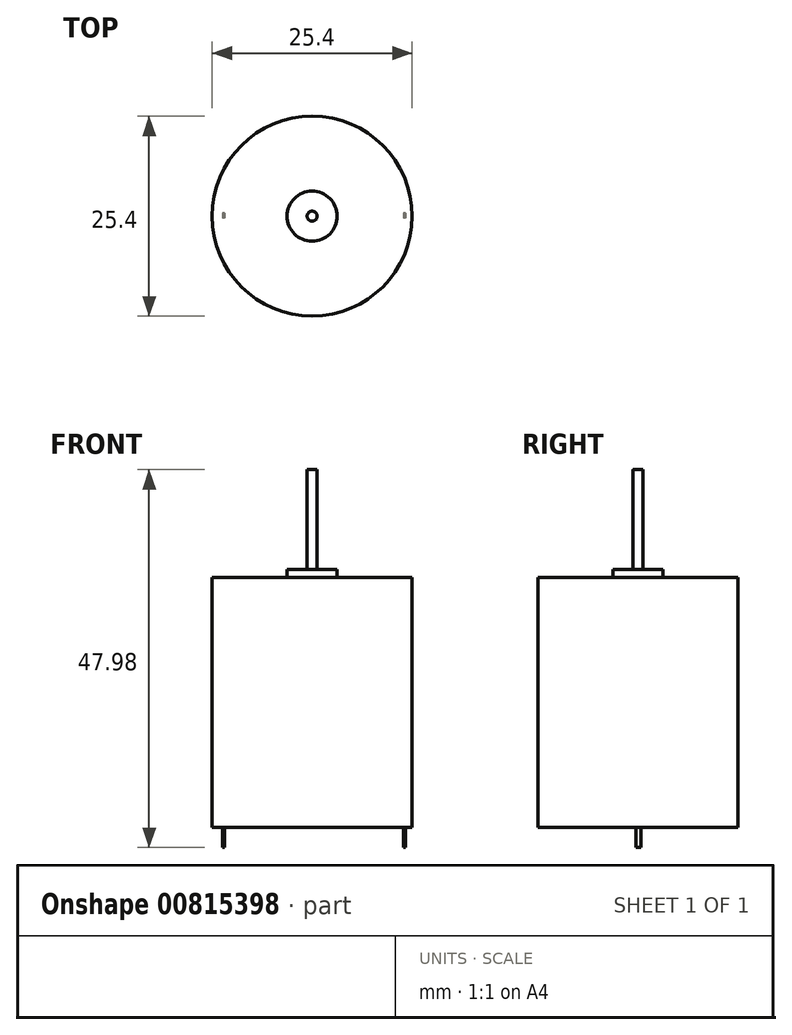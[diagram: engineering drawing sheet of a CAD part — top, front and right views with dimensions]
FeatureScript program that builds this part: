
annotation { "Feature Type Name" : "Feature", "Feature Type Description" : "" }
export const myFeature = defineFeature(function(context is Context, id is Id, definition is map)
    precondition{}
    {
        {
            var Q0;
            Q0=qCreatedBy(makeId("Top.planeOp"),FACE);
            var sketch = newSketch(context, id + "F0", { "sketchPlane" : qUnion([Q0])});
            skCircle(sketch, "E0", {"center": v(0, 0) * mm, "radius": 12.7 * mm});
            skSolve(sketch);
        }
        {
            var Q0;
            Q0=qSketchRegion(id+"F0",true);
            extrude(context, id + "F1", {"entities" : qUnion([Q0]), "depth" : 31.75 * mm});
        }
        {
            var Q0;
            Q0=makeQuery(id+"F1.opExtrude","CAP_FACE",FACE,{"disambiguationData":[OSD([sQuery(id+"F0.wireOp",EDGE,"E0")])],"isStart":false});
            var sketch = newSketch(context, id + "F2", { "sketchPlane" : qUnion([Q0])});
            skCircle(sketch, "E1", {"center": v(0, 0) * mm, "radius": 3.18 * mm});
            skSolve(sketch);
        }
        {
            var Q0;
            Q0=qSketchRegion(id+"F2",true);
            extrude(context, id + "F3", {"entities" : qUnion([Q0]), "operationType" : NewBodyOperationType.ADD, "depth" : 0.99 * mm});
        }
        {
            var Q0;
            Q0=makeQuery(id+"F3.opExtrude","CAP_FACE",FACE,{"disambiguationData":[OSD([sQuery(id+"F2.wireOp",EDGE,"E1")])],"isStart":false});
            var sketch = newSketch(context, id + "F4", { "sketchPlane" : qUnion([Q0])});
            skCircle(sketch, "E2", {"center": v(0, 0) * mm, "radius": 0.64 * mm});
            skSolve(sketch);
        }
        {
            var Q0;
            Q0=makeQuery(id+"F4.imprint","IMPRINT",FACE,{"disambiguationData":[TD([[makeQuery(id+"F4.imprint","IMPRINT",EDGE,{"derivedFrom":sQuery(id+"F4.wireOp",EDGE,"E2")}),1.0]])]});
            extrude(context, id + "F5", {"entities" : qUnion([Q0]), "depth" : 12.7 * mm});
        }
        {
            var Q0;
            Q0=makeQuery(id+"F1.opExtrude","CAP_FACE",FACE,{"disambiguationData":[OSD([sQuery(id+"F0.wireOp",EDGE,"E0")])],"isStart":true});
            var sketch = newSketch(context, id + "F6", { "sketchPlane" : qUnion([Q0])});
            skLineSegment(sketch, "E3.bottom", {"start": v(11.83, -0.37) * mm, "end": v(11.58, -0.37) * mm});
            skLineSegment(sketch, "E3.top", {"start": v(11.83, 0.26) * mm, "end": v(11.58, 0.26) * mm});
            skLineSegment(sketch, "E3.left", {"start": v(11.83, -0.37) * mm, "end": v(11.83, 0.26) * mm});
            skLineSegment(sketch, "E3.right", {"start": v(11.58, -0.37) * mm, "end": v(11.58, 0.26) * mm});
            skLineSegment(sketch, "E4.bottom", {"start": v(-11.1, -0.37) * mm, "end": v(-11.35, -0.37) * mm});
            skLineSegment(sketch, "E4.top", {"start": v(-11.1, 0.26) * mm, "end": v(-11.35, 0.26) * mm});
            skLineSegment(sketch, "E4.left", {"start": v(-11.1, -0.37) * mm, "end": v(-11.1, 0.26) * mm});
            skLineSegment(sketch, "E4.right", {"start": v(-11.35, -0.37) * mm, "end": v(-11.35, 0.26) * mm});
            skSolve(sketch);
        }
        {
            var Q0;
            Q0=qSketchRegion(id+"F6",true);
            extrude(context, id + "F7", {"entities" : qUnion([Q0]), "operationType" : NewBodyOperationType.ADD, "depth" : 2.54 * mm});
        }
    });
